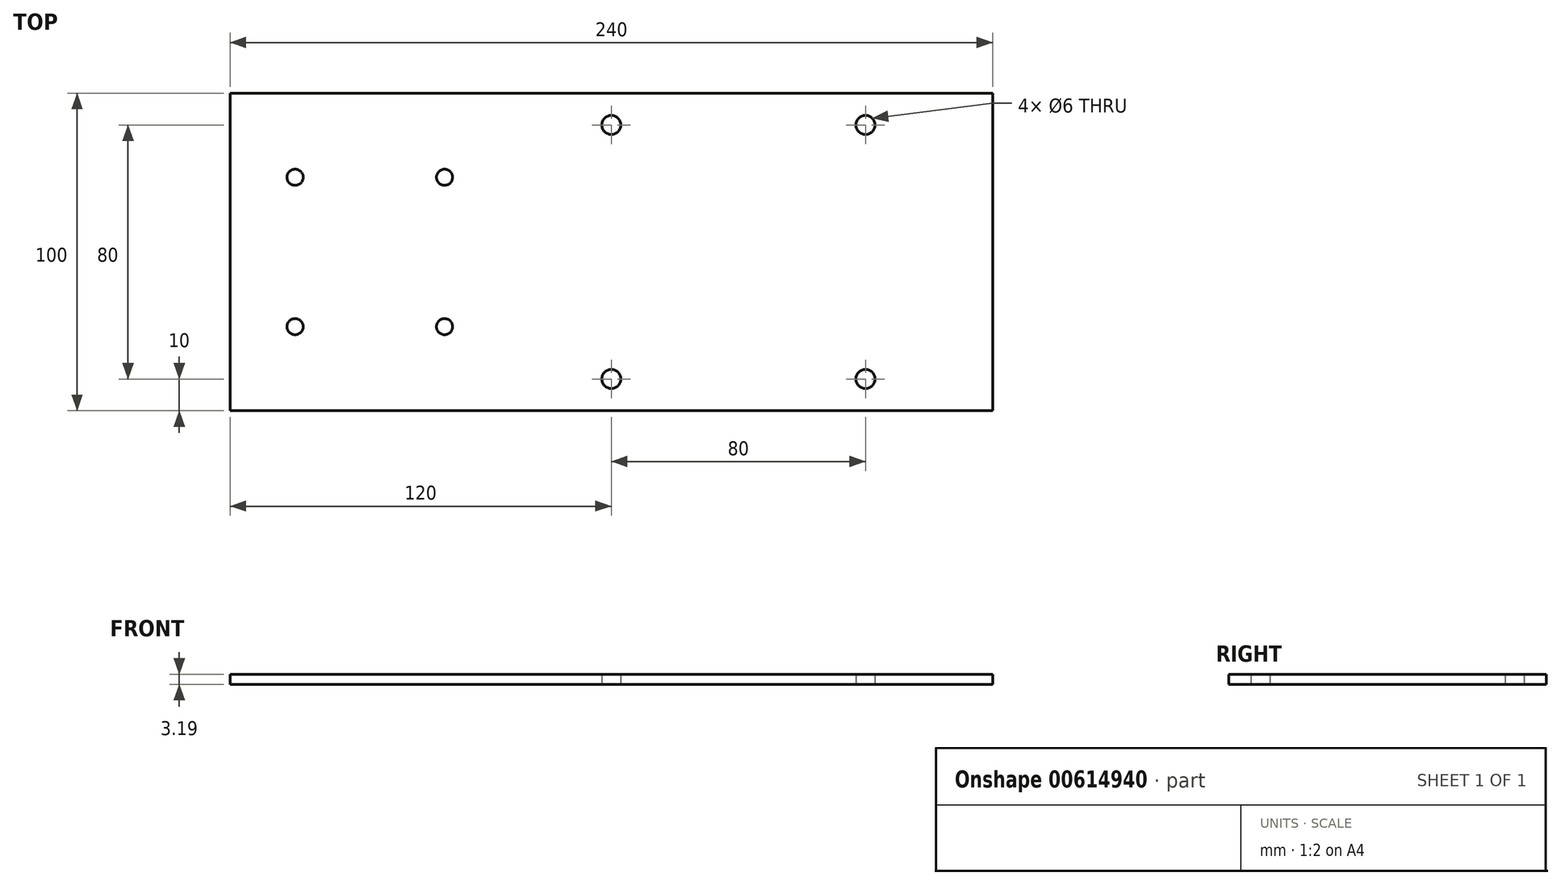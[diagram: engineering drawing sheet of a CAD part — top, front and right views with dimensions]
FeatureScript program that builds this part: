
annotation { "Feature Type Name" : "Feature", "Feature Type Description" : "" }
export const myFeature = defineFeature(function(context is Context, id is Id, definition is map)
    precondition{}
    {
        {
            var Q0;
            Q0=qCreatedBy(makeId("Top.planeOp"),FACE);
            var sketch = newSketch(context, id + "F0", { "sketchPlane" : qUnion([Q0])});
            skLineSegment(sketch, "E0.bottom", {"start": v(100, 50) * mm, "end": v(-100, 50) * mm});
            skLineSegment(sketch, "E0.top", {"start": v(100, -50) * mm, "end": v(-100, -50) * mm});
            skLineSegment(sketch, "E0.left", {"start": v(100, 50) * mm, "end": v(100, -50) * mm});
            skLineSegment(sketch, "E0.right", {"start": v(-100, 50) * mm, "end": v(-100, -50) * mm});
            skPoint(sketch, "E0.middle", {"position": v(0, 0) * mm});
            skLineSegment(sketch, "E1", {"start": v(0, 0) * mm, "end": v(-60, 0) * mm});
            skLineSegment(sketch, "E2", {"start": v(0, 0) * mm, "end": v(60, 0) * mm});
            skLineSegment(sketch, "E3.bottom", {"start": v(-31.47, 28.53) * mm, "end": v(-88.52, 28.53) * mm});
            skLineSegment(sketch, "E3.top", {"start": v(-31.47, -28.52) * mm, "end": v(-88.53, -28.52) * mm});
            skLineSegment(sketch, "E3.left", {"start": v(-31.47, 28.53) * mm, "end": v(-31.48, -28.53) * mm});
            skLineSegment(sketch, "E3.right", {"start": v(-88.52, 28.53) * mm, "end": v(-88.52, -28.52) * mm});
            skPoint(sketch, "E3.middle", {"position": v(-60, 0) * mm});
            skLineSegment(sketch, "E4.bottom", {"start": v(100, -40) * mm, "end": v(20, -40) * mm});
            skLineSegment(sketch, "E4.top", {"start": v(100, 40) * mm, "end": v(20, 40) * mm});
            skLineSegment(sketch, "E4.left", {"start": v(100, -40) * mm, "end": v(100, 40) * mm});
            skLineSegment(sketch, "E4.right", {"start": v(20, -40) * mm, "end": v(20, 40) * mm});
            skPoint(sketch, "E4.middle", {"position": v(60, 0) * mm});
            skCircle(sketch, "E5", {"center": v(20, -40) * mm, "radius": 3 * mm});
            skLineSegment(sketch, "E6.bottom", {"start": v(100, -50) * mm, "end": v(140, -50) * mm});
            skLineSegment(sketch, "E6.top", {"start": v(100, 50) * mm, "end": v(140, 50) * mm});
            skLineSegment(sketch, "E6.left", {"start": v(100, -50) * mm, "end": v(100, 50) * mm});
            skLineSegment(sketch, "E6.right", {"start": v(140, -50) * mm, "end": v(140, 50) * mm});
            skLineSegment(sketch, "E7", {"start": v(60, -40) * mm, "end": v(60, 40) * mm});
            skLineSegment(sketch, "E8", {"start": v(60, 40) * mm, "end": v(60, 0) * mm});
            skLineSegment(sketch, "E9", {"start": v(20, 0) * mm, "end": v(100, 0) * mm});
            skCircle(sketch, "E10.MirrorC", {"center": v(100, -40) * mm, "radius": 3 * mm});
            skCircle(sketch, "E11.MirrorC", {"center": v(100, 40) * mm, "radius": 3 * mm});
            skCircle(sketch, "E12.MirrorC", {"center": v(20, 40) * mm, "radius": 3 * mm});
            skSolve(sketch);
        }
        {
            var Q0;
            Q0 = qSketchRegion(id + "F0", true);
            var Q1;
            {var subQ3=sQuery(id+"F0.wireOp",EDGE,"E3.bottom");Q1=makeQuery(id+"F0.imprint","IMPRINT",FACE,{"disambiguationData":[TD([[makeQuery(id+"F0.imprint","IMPRINT",EDGE,{"derivedFrom":subQ3}),1.0]])]});}
            var Q2;
            {var subQ3=sQuery(id+"F0.wireOp",EDGE,"E8");Q2=makeQuery(id+"F0.imprint","IMPRINT",FACE,{"disambiguationData":[TD([[makeQuery(id+"F0.imprint","IMPRINT",EDGE,{"derivedFrom":subQ3}),-1.0]])]});}
            var Q3;
            {var subQ0=sQuery(id+"F0.wireOp",EDGE,"E7");Q3=makeQuery(id+"F0.imprint","IMPRINT",FACE,{"disambiguationData":[TD([[makeQuery(id+"F0.imprint","IMPRINT",EDGE,{"derivedFrom":subQ0}),1.0]])]});}
            var Q4;
            {var subQ1=sQuery(id+"F0.wireOp",EDGE,"E7");Q4=makeQuery(id+"F0.imprint","IMPRINT",FACE,{"disambiguationData":[TD([[makeQuery(id+"F0.imprint","IMPRINT",EDGE,{"derivedFrom":subQ1}),-1.0]])]});}
            var Q5;
            {var subQ1=sQuery(id+"F0.wireOp",EDGE,"E8");Q5=makeQuery(id+"F0.imprint","IMPRINT",FACE,{"disambiguationData":[TD([[makeQuery(id+"F0.imprint","IMPRINT",EDGE,{"derivedFrom":subQ1}),1.0]])]});}
            extrude(context, id + "F1", {"entities" : qUnion([Q0, Q1, Q2, Q3, Q4, Q5]), "depth" : 3.17 * mm, "offsetDistance" : 25 * mm});
        }
        {
            var Q0;
            Q0=makeQuery(id+"F1.opExtrude","CAP_FACE",FACE,{"disambiguationData":[OSD([sQuery(id+"F0.wireOp",EDGE,"E0.bottom"),sQuery(id+"F0.wireOp",EDGE,"E0.top"),sQuery(id+"F0.wireOp",EDGE,"E0.left"),sQuery(id+"F0.wireOp",EDGE,"E0.right")])],"isStart":false});
            var sketch = newSketch(context, id + "F2", { "sketchPlane" : qUnion([Q0])});
            skCircle(sketch, "E13", {"center": v(-60.02, 0) * mm, "radius": 2.74 * mm});
            skLineSegment(sketch, "E14", {"start": v(3.98, 0) * mm, "end": v(-56.02, 0) * mm});
            skLineSegment(sketch, "E15.bottom", {"start": v(-27.5, 28.53) * mm, "end": v(-84.55, 28.53) * mm});
            skLineSegment(sketch, "E15.top", {"start": v(-27.5, -28.52) * mm, "end": v(-84.55, -28.52) * mm});
            skLineSegment(sketch, "E15.left", {"start": v(-27.5, 28.53) * mm, "end": v(-27.5, -28.52) * mm});
            skLineSegment(sketch, "E15.right", {"start": v(-84.55, 28.53) * mm, "end": v(-84.55, -28.52) * mm});
            skPoint(sketch, "E15.middle", {"position": v(-56.02, 0) * mm});
            skLineSegment(sketch, "E16.bottom", {"start": v(-23.26, 32.77) * mm, "end": v(-88.8, 32.77) * mm});
            skLineSegment(sketch, "E16.top", {"start": v(-23.26, -32.77) * mm, "end": v(-88.8, -32.77) * mm});
            skLineSegment(sketch, "E16.left", {"start": v(-23.26, 32.77) * mm, "end": v(-23.26, -32.77) * mm});
            skLineSegment(sketch, "E16.right", {"start": v(-88.8, 32.77) * mm, "end": v(-88.8, -32.77) * mm});
            skLineSegment(sketch, "E17", {"start": v(-27.5, 28.53) * mm, "end": v(-23.26, 32.77) * mm});
            skLineSegment(sketch, "E18", {"start": v(-27.5, 28.53) * mm, "end": v(-27.5, 20.43) * mm});
            skLineSegment(sketch, "E19", {"start": v(-27.5, 20.43) * mm, "end": v(-23.26, 20.43) * mm});
            skLineSegment(sketch, "E20", {"start": v(-23.26, 20.43) * mm, "end": v(-23.26, 32.77) * mm});
            skLineSegment(sketch, "E21.MirrorCS", {"start": v(-27.5, -20.43) * mm, "end": v(-23.25, -20.43) * mm});
            skLineSegment(sketch, "E22.MirrorCS", {"start": v(-23.25, -20.43) * mm, "end": v(-23.25, -32.77) * mm});
            skLineSegment(sketch, "E23", {"start": v(-27.5, -20.43) * mm, "end": v(-27.5, -28.52) * mm});
            skLineSegment(sketch, "E24", {"start": v(-84.55, 28.53) * mm, "end": v(-79.55, 23.52) * mm});
            skCircle(sketch, "E25", {"center": v(-79.55, 23.52) * mm, "radius": 2.55 * mm});
            skLineSegment(sketch, "E26.bottom", {"start": v(-84.55, 28.53) * mm, "end": v(-73.55, 28.53) * mm});
            skLineSegment(sketch, "E26.top", {"start": v(-84.55, 17.53) * mm, "end": v(-78.55, 17.53) * mm});
            skLineSegment(sketch, "E26.left", {"start": v(-84.55, 28.53) * mm, "end": v(-84.55, 17.53) * mm});
            skLineSegment(sketch, "E26.right", {"start": v(-73.55, 28.53) * mm, "end": v(-73.55, 22.53) * mm});
            skPoint(sketch, "E27.visualSharp", {"position": v(-73.55, 17.53) * mm});
            skArc(sketch, "E27.filletArc", {"start": v(-78.55, 17.53) * mm, "mid": v(-75.01, 18.99) * mm, "end": v(-73.55, 22.53) * mm});
            skLineSegment(sketch, "E28", {"start": v(-27.5, 28.53) * mm, "end": v(-32.5, 23.53) * mm});
            skCircle(sketch, "E29", {"center": v(-32.5, 23.53) * mm, "radius": 2.55 * mm});
            skLineSegment(sketch, "E30", {"start": v(-27.5, 20.43) * mm, "end": v(-33.5, 20.43) * mm});
            skLineSegment(sketch, "E31", {"start": v(-38.5, 25.43) * mm, "end": v(-38.5, 28.53) * mm});
            skPoint(sketch, "E32.visualSharp", {"position": v(-38.5, 20.43) * mm});
            skArc(sketch, "E32.filletArc", {"start": v(-38.5, 25.43) * mm, "mid": v(-37.03, 21.9) * mm, "end": v(-33.5, 20.43) * mm});
            skLineSegment(sketch, "E33", {"start": v(-84.55, -28.52) * mm, "end": v(-79.55, -23.53) * mm});
            skLineSegment(sketch, "E34", {"start": v(-73.55, -28.52) * mm, "end": v(-73.55, -22.52) * mm});
            skLineSegment(sketch, "E35", {"start": v(-78.55, -17.52) * mm, "end": v(-84.55, -17.52) * mm});
            skPoint(sketch, "E36.visualSharp", {"position": v(-73.55, -17.52) * mm});
            skArc(sketch, "E36.filletArc", {"start": v(-73.55, -22.52) * mm, "mid": v(-75.01, -18.99) * mm, "end": v(-78.55, -17.52) * mm});
            skCircle(sketch, "E37", {"center": v(-79.55, -23.53) * mm, "radius": 2.55 * mm});
            skLineSegment(sketch, "E38", {"start": v(-27.5, -28.52) * mm, "end": v(-32.5, -23.53) * mm});
            skLineSegment(sketch, "E39", {"start": v(-38.5, -25.43) * mm, "end": v(-38.5, -28.52) * mm});
            skCircle(sketch, "E40", {"center": v(-32.5, -23.53) * mm, "radius": 2.55 * mm});
            skLineSegment(sketch, "E41", {"start": v(-27.5, -20.43) * mm, "end": v(-33.5, -20.43) * mm});
            skLineSegment(sketch, "E42", {"start": v(-47.3, -26.68) * mm, "end": v(-47.3, -26.68) * mm});
            skPoint(sketch, "E43.visualSharp", {"position": v(-38.5, -20.43) * mm});
            skArc(sketch, "E43.filletArc", {"start": v(-33.5, -20.43) * mm, "mid": v(-37.03, -21.9) * mm, "end": v(-38.5, -25.43) * mm});
            skSolve(sketch);
        }
        {
            var Q0;
            Q0=makeQuery(id+"F2.imprint","IMPRINT",FACE,{"disambiguationData":[TD([[makeQuery(id+"F2.imprint","IMPRINT",EDGE,{"derivedFrom":sQuery(id+"F2.wireOp",EDGE,"E25")}),1.0]])]});
            var Q1;
            Q1=makeQuery(id+"F2.imprint","IMPRINT",FACE,{"disambiguationData":[TD([[makeQuery(id+"F2.imprint","IMPRINT",EDGE,{"derivedFrom":sQuery(id+"F2.wireOp",EDGE,"E37")}),1.0]])]});
            var Q2;
            Q2=makeQuery(id+"F2.imprint","IMPRINT",FACE,{"disambiguationData":[TD([[makeQuery(id+"F2.imprint","IMPRINT",EDGE,{"derivedFrom":sQuery(id+"F2.wireOp",EDGE,"E40")}),1.0]])]});
            var Q3;
            Q3=makeQuery(id+"F2.imprint","IMPRINT",FACE,{"disambiguationData":[TD([[makeQuery(id+"F2.imprint","IMPRINT",EDGE,{"derivedFrom":sQuery(id+"F2.wireOp",EDGE,"E29")}),1.0]])]});
            extrude(context, id + "F3", {"entities" : qUnion([Q0, Q1, Q2, Q3]), "operationType" : NewBodyOperationType.ADD, "depth" : 0.01 * mm, "offsetDistance" : 25 * mm});
        }
    });
